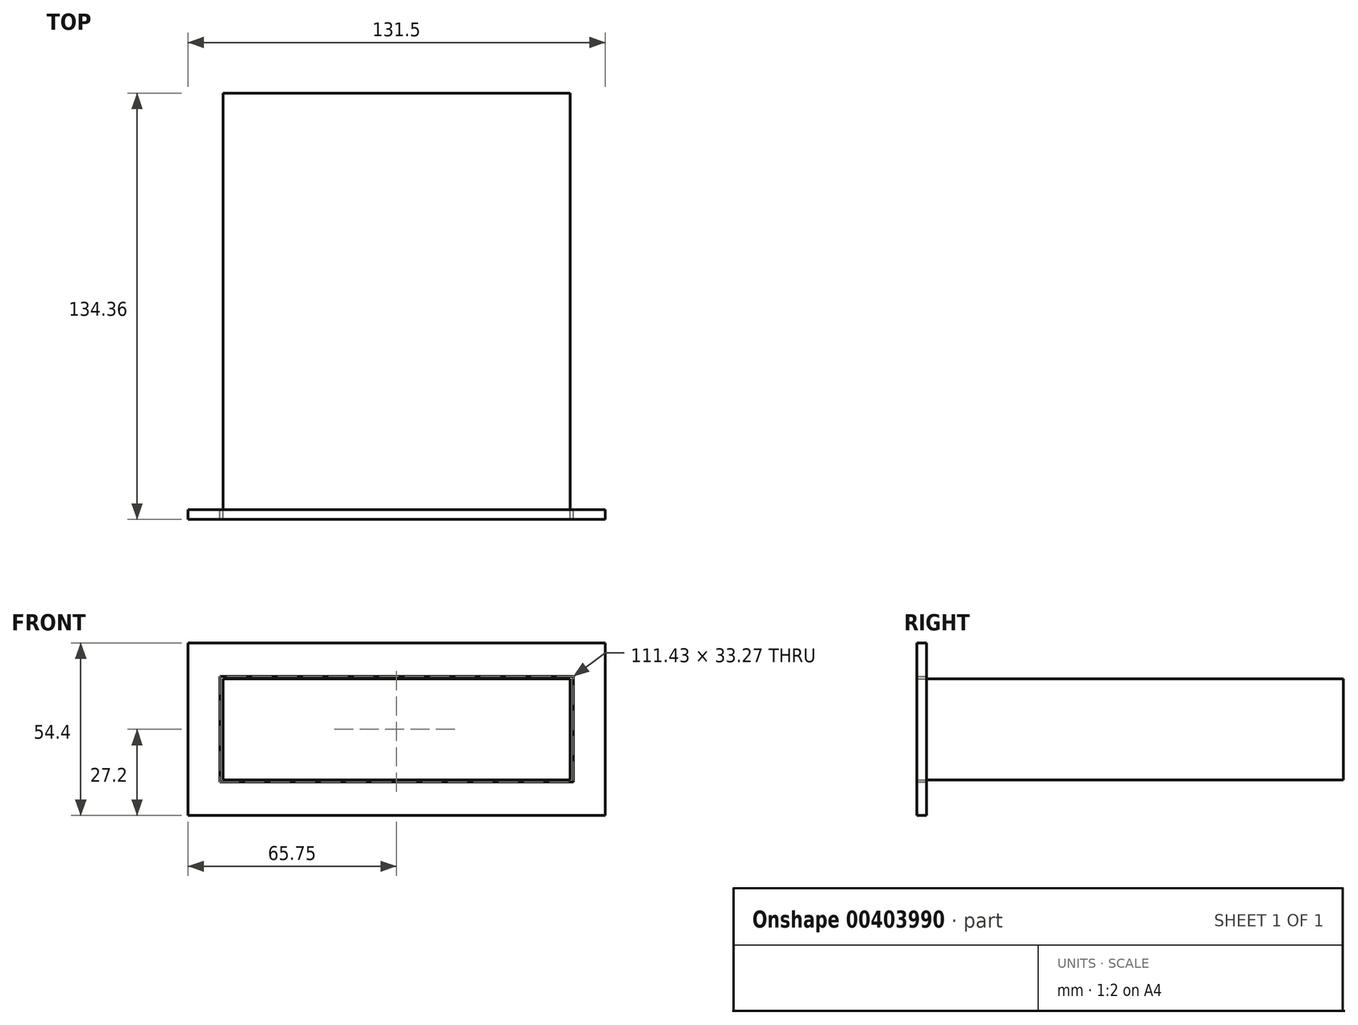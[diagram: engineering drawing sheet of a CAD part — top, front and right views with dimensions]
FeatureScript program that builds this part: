
annotation { "Feature Type Name" : "Feature", "Feature Type Description" : "" }
export const myFeature = defineFeature(function(context is Context, id is Id, definition is map)
    precondition{}
    {
        {
            var Q0;
            Q0=qCreatedBy(makeId("Front.planeOp"),FACE);
            var sketch = newSketch(context, id + "F0", { "sketchPlane" : qUnion([Q0])});
            skLineSegment(sketch, "E0.bottom", {"start": v(-65.75, 27.2) * mm, "end": v(65.75, 27.2) * mm});
            skLineSegment(sketch, "E0.top", {"start": v(-65.75, -27.2) * mm, "end": v(65.75, -27.2) * mm});
            skLineSegment(sketch, "E0.left", {"start": v(-65.75, 27.2) * mm, "end": v(-65.75, -27.2) * mm});
            skLineSegment(sketch, "E0.right", {"start": v(65.75, 27.2) * mm, "end": v(65.75, -27.2) * mm});
            skPoint(sketch, "E0.middle", {"position": v(0, 0) * mm});
            skLineSegment(sketch, "E1.bottom", {"start": v(-55.72, 16.64) * mm, "end": v(55.72, 16.64) * mm});
            skLineSegment(sketch, "E1.top", {"start": v(-55.72, -16.64) * mm, "end": v(55.72, -16.64) * mm});
            skLineSegment(sketch, "E1.left", {"start": v(-55.72, 16.64) * mm, "end": v(-55.72, -16.64) * mm});
            skLineSegment(sketch, "E1.right", {"start": v(55.72, 16.64) * mm, "end": v(55.72, -16.64) * mm});
            skLineSegment(sketch, "E2.bottom", {"start": v(54.7, 15.93) * mm, "end": v(-54.7, 15.93) * mm});
            skLineSegment(sketch, "E2.top", {"start": v(54.7, -15.93) * mm, "end": v(-54.7, -15.93) * mm});
            skLineSegment(sketch, "E2.left", {"start": v(54.7, 15.93) * mm, "end": v(54.7, -15.93) * mm});
            skLineSegment(sketch, "E2.right", {"start": v(-54.7, 15.93) * mm, "end": v(-54.7, -15.93) * mm});
            skSolve(sketch);
        }
        {
            var Q0;
            Q0=makeQuery(id+"F0.imprint","IMPRINT",FACE,{"disambiguationData":[TD([[makeQuery(id+"F0.imprint","IMPRINT",EDGE,{"derivedFrom":sQuery(id+"F0.wireOp",EDGE,"E0.bottom")}),-1.0]])]});
            var Q1;
            Q1=makeQuery(id+"F0.imprint","IMPRINT",FACE,{"disambiguationData":[TD([[makeQuery(id+"F0.imprint","IMPRINT",EDGE,{"derivedFrom":sQuery(id+"F0.wireOp",EDGE,"E2.bottom")}),1.0]])]});
            extrude(context, id + "F1", {"entities" : qUnion([Q0, Q1]), "endBound" : BoundingType.SYMMETRIC, "depth" : 3.05 * mm});
        }
        {
            var Q0;
            Q0=makeQuery(id+"F1.opExtrude","CAP_FACE",FACE,{"disambiguationData":[OSD([sQuery(id+"F0.wireOp",EDGE,"E2.bottom"),sQuery(id+"F0.wireOp",EDGE,"E2.top"),sQuery(id+"F0.wireOp",EDGE,"E2.left"),sQuery(id+"F0.wireOp",EDGE,"E2.right")])],"isStart":true});
            var sketch = newSketch(context, id + "F2", { "sketchPlane" : qUnion([Q0])});
            skSolve(sketch);
        }
        {
            var Q0;
            Q0=makeQuery(id+"F2.imprint","IMPRINT",FACE,{"disambiguationData":[TD([[makeQuery(id+"F2.imprint","IMPRINT",EDGE,{"derivedFrom":makeQuery(id+"F1.opExtrude","CAP_EDGE",EDGE,{"disambiguationData":[OSD([sQuery(id+"F0.wireOp",EDGE,"E2.bottom")])],"isStart":true})}),-1.0]])]});
            extrude(context, id + "F3", {"entities" : qUnion([Q0]), "operationType" : NewBodyOperationType.ADD, "depth" : 131.32 * mm, "offsetDistance" : 25.4 * mm});
        }
    });
